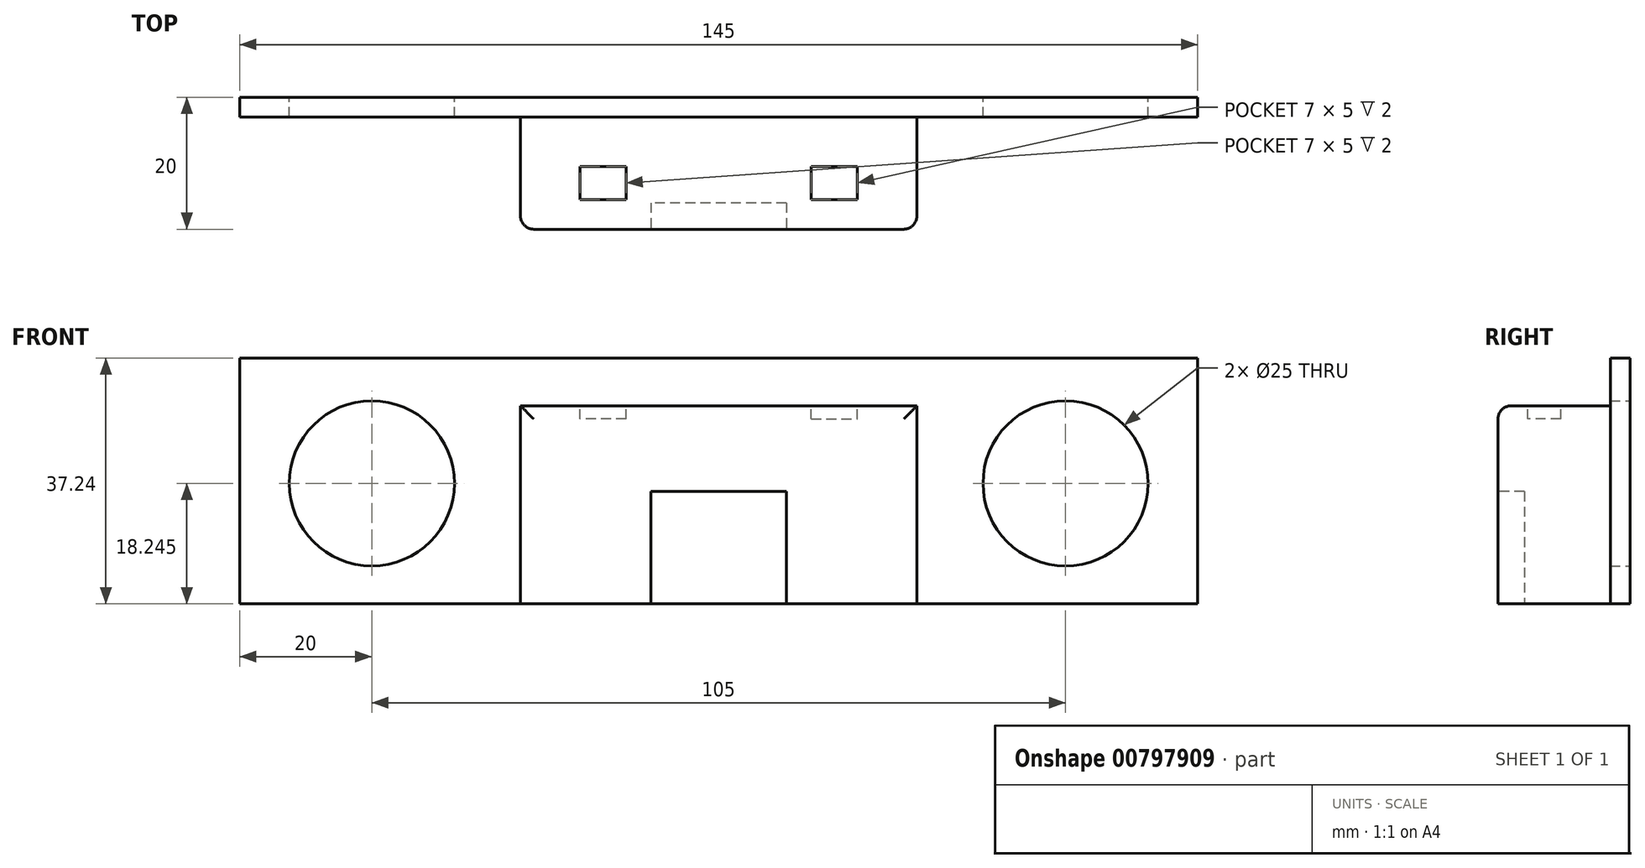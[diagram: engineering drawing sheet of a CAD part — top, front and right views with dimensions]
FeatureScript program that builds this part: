
annotation { "Feature Type Name" : "Feature", "Feature Type Description" : "" }
export const myFeature = defineFeature(function(context is Context, id is Id, definition is map)
    precondition{}
    {
        {
            var Q0;
            Q0=qCreatedBy(makeId("Front.planeOp"),FACE);
            var sketch = newSketch(context, id + "F0", { "sketchPlane" : qUnion([Q0])});
            skLineSegment(sketch, "E0.bottom", {"start": v(72.5, 18.62) * mm, "end": v(-72.5, 18.62) * mm});
            skLineSegment(sketch, "E0.top", {"start": v(72.5, -18.62) * mm, "end": v(-72.5, -18.62) * mm});
            skLineSegment(sketch, "E0.left", {"start": v(72.5, 18.62) * mm, "end": v(72.5, -18.62) * mm});
            skLineSegment(sketch, "E0.right", {"start": v(-72.5, 18.62) * mm, "end": v(-72.5, -18.62) * mm});
            skPoint(sketch, "E0.middle", {"position": v(0, 0) * mm});
            skCircle(sketch, "E1", {"center": v(52.5, -0.37) * mm, "radius": 12.5 * mm});
            skCircle(sketch, "E2", {"center": v(-52.5, -0.37) * mm, "radius": 12.5 * mm});
            skSolve(sketch);
        }
        {
            var Q0;
            Q0=qSketchRegion(id+"F0",true);
            extrude(context, id + "F1", {"entities" : qUnion([Q0]), "depth" : 3 * mm});
        }
        {
            var Q0;
            Q0=makeQuery(id+"F1.opExtrude","CAP_FACE",FACE,{"disambiguationData":[OSD([sQuery(id+"F0.wireOp",EDGE,"E0.bottom"),sQuery(id+"F0.wireOp",EDGE,"E0.top"),sQuery(id+"F0.wireOp",EDGE,"E0.left"),sQuery(id+"F0.wireOp",EDGE,"E0.right"),sQuery(id+"F0.wireOp",EDGE,"sOKRK9WS-TzGH-iPKk-9lGy-1haYnsqfv4Nf"),sQuery(id+"F0.wireOp",EDGE,"94ZFEkxM-q5Sw-y5fY-uU9Y-FHWCruAk6SLc")])],"isStart":false});
            var sketch = newSketch(context, id + "F2", { "sketchPlane" : qUnion([Q0])});
            skLineSegment(sketch, "E3.bottom", {"start": v(-30, 11.37) * mm, "end": v(30, 11.38) * mm});
            skLineSegment(sketch, "E3.top", {"start": v(-30, -18.63) * mm, "end": v(30, -18.62) * mm});
            skLineSegment(sketch, "E3.left", {"start": v(-30, 11.37) * mm, "end": v(-30, -18.63) * mm});
            skLineSegment(sketch, "E3.right", {"start": v(30, 11.38) * mm, "end": v(30, -18.62) * mm});
            skSolve(sketch);
        }
        {
            var Q0;
            Q0=qSketchRegion(id+"F2",true);
            extrude(context, id + "F3", {"entities" : qUnion([Q0]), "operationType" : NewBodyOperationType.ADD, "depth" : 17 * mm});
        }
        {
            var Q0;
            Q0=makeQuery(id+"F3.opExtrude","SWEPT_FACE",FACE,{"disambiguationData":[OSD([sQuery(id+"F2.wireOp",EDGE,"E3.bottom")])]});
            var sketch = newSketch(context, id + "F4", { "sketchPlane" : qUnion([Q0])});
            skLineSegment(sketch, "E4.bottom", {"start": v(17.5, -13) * mm, "end": v(-17.5, -13) * mm, "construction": true});
            skLineSegment(sketch, "E4.top", {"start": v(17.5, -13) * mm, "end": v(-17.5, -13) * mm, "construction": true});
            skLineSegment(sketch, "E4.left", {"start": v(17.5, -13) * mm, "end": v(17.5, -13) * mm});
            skLineSegment(sketch, "E4.right", {"start": v(-17.5, -13) * mm, "end": v(-17.5, -13) * mm});
            skPoint(sketch, "E4.middle", {"position": v(0, -13) * mm});
            skLineSegment(sketch, "E5.bottom", {"start": v(-14, -10.5) * mm, "end": v(-21, -10.5) * mm});
            skLineSegment(sketch, "E5.top", {"start": v(-14, -15.5) * mm, "end": v(-21, -15.5) * mm});
            skLineSegment(sketch, "E5.left", {"start": v(-14, -10.5) * mm, "end": v(-14, -15.5) * mm});
            skLineSegment(sketch, "E5.right", {"start": v(-21, -10.5) * mm, "end": v(-21, -15.5) * mm});
            skPoint(sketch, "E5.middle", {"position": v(-17.5, -13) * mm});
            skLineSegment(sketch, "E6.bottom", {"start": v(14, -10.5) * mm, "end": v(21, -10.5) * mm});
            skLineSegment(sketch, "E6.top", {"start": v(14, -15.5) * mm, "end": v(21, -15.5) * mm});
            skLineSegment(sketch, "E6.left", {"start": v(14, -10.5) * mm, "end": v(14, -15.5) * mm});
            skLineSegment(sketch, "E6.right", {"start": v(21, -10.5) * mm, "end": v(21, -15.5) * mm});
            skPoint(sketch, "E6.middle", {"position": v(17.5, -13) * mm});
            skSolve(sketch);
        }
        {
            var Q0;
            Q0=qSketchRegion(id+"F4",true);
            extrude(context, id + "F5", {"entities" : qUnion([Q0]), "operationType" : NewBodyOperationType.REMOVE, "oppositeDirection" : true, "depth" : 2 * mm});
        }
        {
            var Q0;
            Q0=makeQuery(id+"F3.opExtrude","CAP_EDGE",EDGE,{"disambiguationData":[OSD([sQuery(id+"F2.wireOp",EDGE,"E3.bottom")])],"isStart":true});
            var Q1;
            Q1=makeQuery(id+"F3.opExtrude","CAP_EDGE",EDGE,{"disambiguationData":[OSD([sQuery(id+"F2.wireOp",EDGE,"E3.right")])],"isStart":true});
            var Q2;
            Q2=makeQuery(id+"F3.opExtrude","CAP_EDGE",EDGE,{"disambiguationData":[OSD([sQuery(id+"F2.wireOp",EDGE,"E3.left")])],"isStart":true});
            var Q3;
            Q3=makeQuery(id+"F3.opExtrude","CAP_EDGE",EDGE,{"disambiguationData":[OSD([sQuery(id+"F2.wireOp",EDGE,"E3.left")])],"isStart":false});
            var Q4;
            Q4=makeQuery(id+"F3.opExtrude","CAP_EDGE",EDGE,{"disambiguationData":[OSD([sQuery(id+"F2.wireOp",EDGE,"E3.bottom")])],"isStart":false});
            var Q5;
            Q5=makeQuery(id+"F3.opExtrude","CAP_EDGE",EDGE,{"disambiguationData":[OSD([sQuery(id+"F2.wireOp",EDGE,"E3.right")])],"isStart":false});
            fillet(context, id + "F6", {"entities" : qUnion([Q0, Q1, Q2, Q3, Q4, Q5]), "radius" : 2 * mm, "tangentPropagation" : true, "allowEdgeOverflow" : false});
        }
        {
            var Q0;
            Q0=makeQuery(id+"F3.opExtrude","CAP_FACE",FACE,{"disambiguationData":[OSD([sQuery(id+"F2.wireOp",EDGE,"E3.bottom"),sQuery(id+"F2.wireOp",EDGE,"E3.top"),sQuery(id+"F2.wireOp",EDGE,"E3.left"),sQuery(id+"F2.wireOp",EDGE,"E3.right")])],"isStart":false});
            var sketch = newSketch(context, id + "F7", { "sketchPlane" : qUnion([Q0])});
            skLineSegment(sketch, "E7.bottom", {"start": v(10.25, -1.62) * mm, "end": v(-10.25, -1.62) * mm});
            skLineSegment(sketch, "E7.top", {"start": v(10.25, -18.62) * mm, "end": v(-10.25, -18.62) * mm});
            skLineSegment(sketch, "E7.left", {"start": v(10.25, -1.62) * mm, "end": v(10.25, -18.62) * mm});
            skLineSegment(sketch, "E7.right", {"start": v(-10.25, -1.62) * mm, "end": v(-10.25, -18.62) * mm});
            skPoint(sketch, "E7.middle", {"position": v(0, -10.12) * mm});
            skSolve(sketch);
        }
        {
            var Q0;
            Q0=qSketchRegion(id+"F7",true);
            extrude(context, id + "F8", {"entities" : qUnion([Q0]), "operationType" : NewBodyOperationType.REMOVE, "oppositeDirection" : true, "depth" : 4 * mm, "offsetDistance" : 25 * mm});
        }
    });
